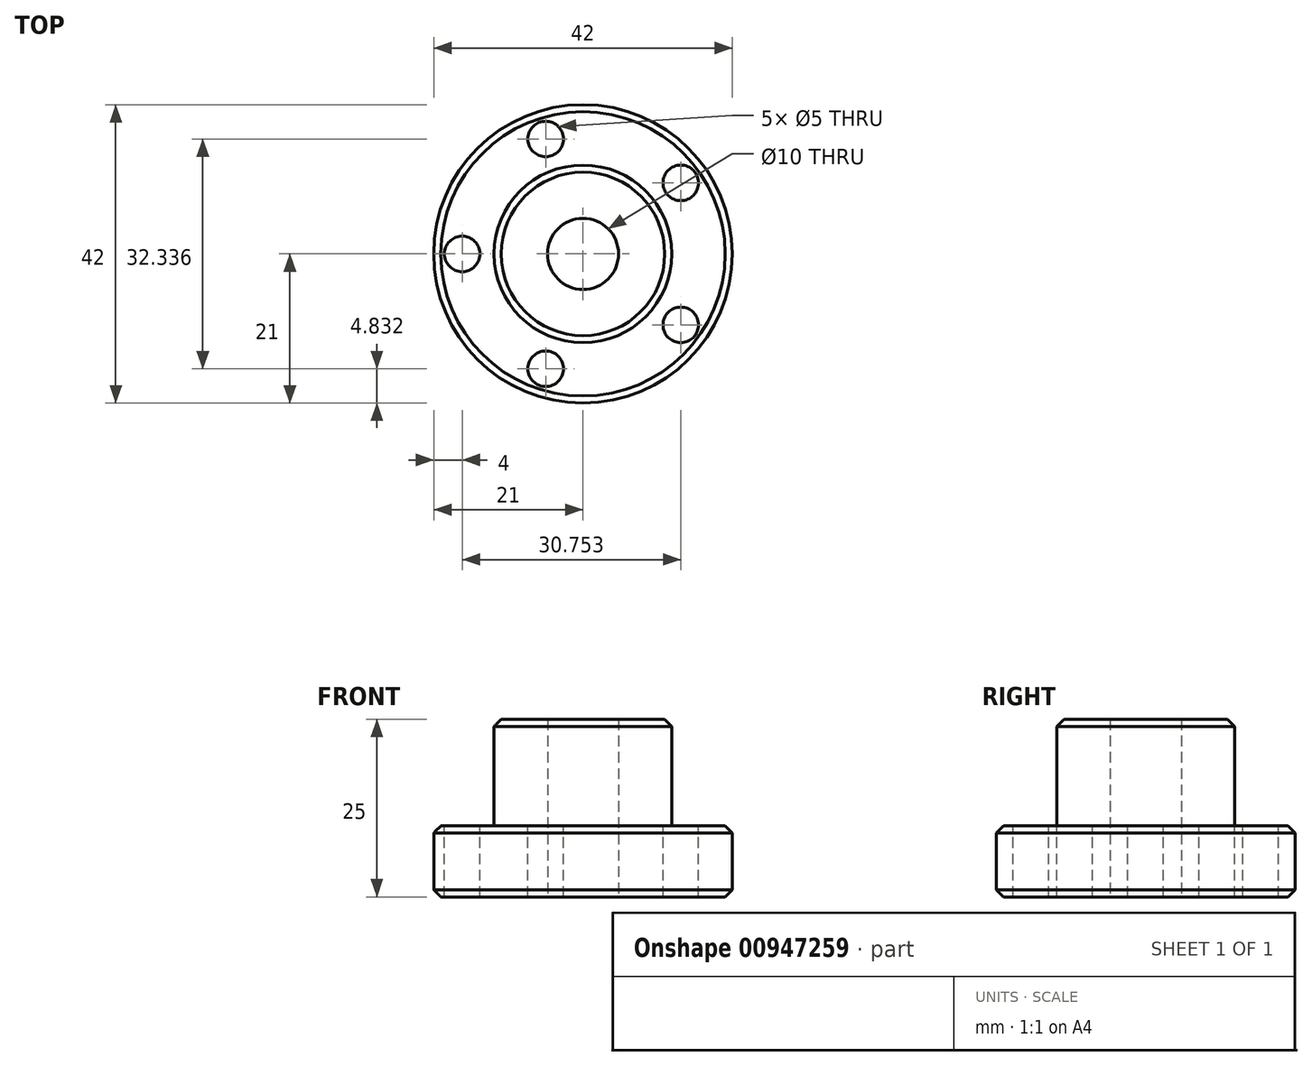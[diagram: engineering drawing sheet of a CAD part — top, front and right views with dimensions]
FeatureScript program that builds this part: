
annotation { "Feature Type Name" : "Feature", "Feature Type Description" : "" }
export const myFeature = defineFeature(function(context is Context, id is Id, definition is map)
    precondition{}
    {
        {
            var Q0;
            Q0=qCreatedBy(makeId("Front.planeOp"),FACE);
            var sketch = newSketch(context, id + "F0", { "sketchPlane" : qUnion([Q0])});
            skLineSegment(sketch, "E0", {"start": v(0, 25) * mm, "end": v(-12.5, 25) * mm});
            skLineSegment(sketch, "E1", {"start": v(-12.5, 25) * mm, "end": v(-12.5, 16) * mm});
            skLineSegment(sketch, "E2", {"start": v(-12.5, 16) * mm, "end": v(-12.5, 16) * mm});
            skLineSegment(sketch, "E3", {"start": v(-12.5, 16) * mm, "end": v(-12.5, 10) * mm});
            skLineSegment(sketch, "E4", {"start": v(-12.5, 10) * mm, "end": v(-21, 10) * mm});
            skLineSegment(sketch, "E5", {"start": v(-21, 10) * mm, "end": v(-21, 0) * mm});
            skLineSegment(sketch, "E6", {"start": v(-21, 0) * mm, "end": v(0, 0) * mm});
            skLineSegment(sketch, "E7", {"start": v(0, 0) * mm, "end": v(0, 25) * mm});
            skLineSegment(sketch, "E8", {"start": v(-12.5, 24) * mm, "end": v(-11.5, 25) * mm});
            skLineSegment(sketch, "E9", {"start": v(-20, 10) * mm, "end": v(-21, 9) * mm});
            skLineSegment(sketch, "E10", {"start": v(-21, 1) * mm, "end": v(-20, 0) * mm});
            skLineSegment(sketch, "E11", {"start": v(-5, 25) * mm, "end": v(-5, 0) * mm});
            skSolve(sketch);
        }
        {
            var Q0;
            {var subQ0=sQuery(id+"F0.wireOp",EDGE,"E3");Q0=makeQuery(id+"F0.imprint","IMPRINT",FACE,{"disambiguationData":[TD([[makeQuery(id+"F0.imprint","IMPRINT",EDGE,{"derivedFrom":subQ0}),1.0]])]});}
            var Q1;
            Q1=sQuery(id+"F0.wireOp",EDGE,"E7");
            revolve(context, id + "F1", {"surfaceOperationType" : NewSurfaceOperationType.NEW, "entities" : qUnion([Q0]), "axis" : qUnion([Q1]), "revolveType" : RevolveType.FULL});
        }
        {
            var Q0;
            Q0=makeQuery(id+"F1.opRevolve","SWEPT_FACE",FACE,{"disambiguationData":[OSD([sQuery(id+"F0.wireOp",EDGE,"E4")])]});
            var sketch = newSketch(context, id + "F2", { "sketchPlane" : qUnion([Q0])});
            skCircle(sketch, "E12.cCircle", {"center": v(0, 0) * mm, "radius": 17 * mm, "construction": true});
            skLineSegment(sketch, "E12.0", {"start": v(-17, 0) * mm, "end": v(-5.25, 16.17) * mm, "construction": true});
            skLineSegment(sketch, "E12.1", {"start": v(-5.25, 16.17) * mm, "end": v(13.75, 10) * mm, "construction": true});
            skLineSegment(sketch, "E12.2", {"start": v(13.75, 10) * mm, "end": v(13.75, -10) * mm, "construction": true});
            skLineSegment(sketch, "E12.3", {"start": v(13.75, -10) * mm, "end": v(-5.25, -16.17) * mm, "construction": true});
            skLineSegment(sketch, "E12.4", {"start": v(-5.25, -16.17) * mm, "end": v(-17, 0) * mm, "construction": true});
            skSolve(sketch);
        }
        {
            var Q0;
            Q0=sQuery(id+"F2.wireOp",VERTEX,"E12.0.start");
            var Q1;
            Q1=sQuery(id+"F2.wireOp",VERTEX,"E12.0.end");
            var Q2;
            Q2=sQuery(id+"F2.wireOp",VERTEX,"E12.1.end");
            var Q3;
            Q3=sQuery(id+"F2.wireOp",VERTEX,"E12.2.end");
            var Q4;
            Q4=sQuery(id+"F2.wireOp",VERTEX,"E12.3.end");
            var Q5;
            Q5=makeQuery(id+"F1.opRevolve","SWEPT_BODY",BODY,{"disambiguationData":[OSD([sQuery(id+"F0.wireOp",EDGE,"E0"),sQuery(id+"F0.wireOp",EDGE,"E1"),sQuery(id+"F0.wireOp",EDGE,"E3"),sQuery(id+"F0.wireOp",EDGE,"E4"),sQuery(id+"F0.wireOp",EDGE,"E5"),sQuery(id+"F0.wireOp",EDGE,"E6"),sQuery(id+"F0.wireOp",EDGE,"E8"),sQuery(id+"F0.wireOp",EDGE,"E9"),sQuery(id+"F0.wireOp",EDGE,"E10"),sQuery(id+"F0.wireOp",EDGE,"E11")])]});
            hole(context, id + "F3", {"style" : HoleStyle.SIMPLE, "endStyle" : HoleEndStyle.BLIND, "holeDiameter" : 5 * mm, "majorDiameter" : 5 * mm, "holeDepth" : 20 * mm, "isTappedThrough" : true, "tappedDepth" : 20 * mm, "tapClearance" : 3, "startFromSketch" : true, "locations" : qUnion([Q0, Q1, Q2, Q3, Q4]), "scope" : qUnion([Q5])});
        }
    });
